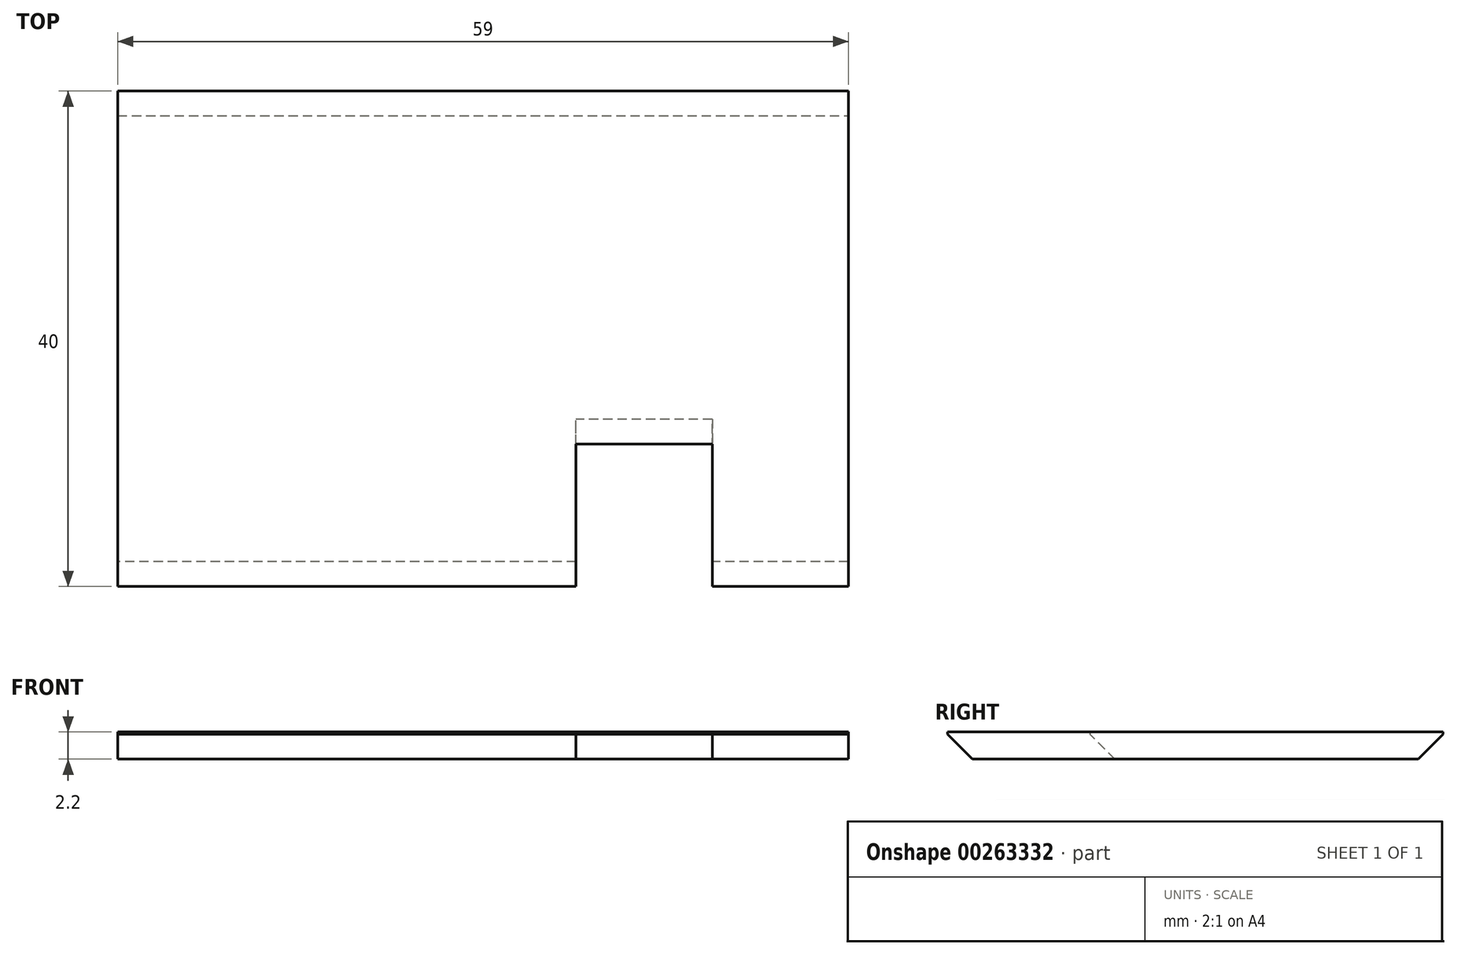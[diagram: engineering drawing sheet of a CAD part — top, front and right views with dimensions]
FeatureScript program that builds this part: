
annotation { "Feature Type Name" : "Feature", "Feature Type Description" : "" }
export const myFeature = defineFeature(function(context is Context, id is Id, definition is map)
    precondition{}
    {
        {
            var Q0;
            Q0=qCreatedBy(makeId("Top.planeOp"),FACE);
            var sketch = newSketch(context, id + "F0", { "sketchPlane" : qUnion([Q0])});
            skLineSegment(sketch, "E0.bottom", {"start": v(-59.12, 38.17) * mm, "end": v(-0.12, 38.17) * mm});
            skLineSegment(sketch, "E0.top", {"start": v(-59.12, -1.83) * mm, "end": v(-0.12, -1.83) * mm});
            skLineSegment(sketch, "E0.left", {"start": v(-59.12, 38.17) * mm, "end": v(-59.12, -1.83) * mm});
            skLineSegment(sketch, "E0.right", {"start": v(-0.12, 38.17) * mm, "end": v(-0.12, -1.83) * mm});
            skLineSegment(sketch, "E1.bottom", {"start": v(-22.12, -1.83) * mm, "end": v(-11.12, -1.83) * mm});
            skLineSegment(sketch, "E1.top", {"start": v(-22.12, 9.67) * mm, "end": v(-11.12, 9.67) * mm});
            skLineSegment(sketch, "E1.left", {"start": v(-22.12, -1.83) * mm, "end": v(-22.12, 9.67) * mm});
            skLineSegment(sketch, "E1.right", {"start": v(-11.12, -1.83) * mm, "end": v(-11.12, 9.67) * mm});
            skSolve(sketch);
        }
        {
            var Q0;
            Q0=makeQuery(id+"F0.imprint","IMPRINT",FACE,{"disambiguationData":[TD([[makeQuery(id+"F0.imprint","IMPRINT",EDGE,{"derivedFrom":sQuery(id+"F0.wireOp",EDGE,"E0.bottom")}),-1.0]])]});
            extrude(context, id + "F1", {"entities" : qUnion([Q0]), "depth" : 2.2 * mm});
        }
        {
            var Q0;
            Q0=makeQuery(id+"F1.opExtrude","CAP_EDGE",EDGE,{"disambiguationData":[OSD([sQuery(id+"F0.wireOp",EDGE,"E0.bottom")])],"isStart":true});
            var Q1;
            Q1=makeQuery(id+"F1.opExtrude","CAP_EDGE",EDGE,{"disambiguationData":[OSD([sQuery(id+"F0.wireOp",EDGE,"E0.top")])],"isStart":true});
            chamfer(context, id + "F2", {"entities" : qUnion([Q0, Q1]), "width" : 2 * mm, "tangentPropagation" : true});
        }
        {
            var Q0;
            Q0=makeQuery(id+"F1.opExtrude","CAP_EDGE",EDGE,{"disambiguationData":[OSD([sQuery(id+"F0.wireOp",EDGE,"E1.top")])],"isStart":true});
            chamfer(context, id + "F3", {"entities" : qUnion([Q0]), "width" : 2 * mm, "tangentPropagation" : true});
        }
    });
